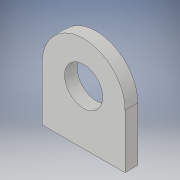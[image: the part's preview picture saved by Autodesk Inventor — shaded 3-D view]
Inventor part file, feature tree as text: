
AUTODESK INVENTOR PART (.ipt)
format: ipt  version: 2019 (Build 230136000, 136)  size: 108,544 bytes
history: native  units: mm
features: other x1, sketch x1, extrude x1, fillet x1, hole x1
ambient origin geometry x8: Origin, YZ Plane, XZ Plane, XY Plane, X Axis, Y Axis, Z Axis, Center Point
bodies: Body1 (feature_tree)
feature tree (5):
  other  "Bryła1"
  sketch  "Szkic1"
  extrude  "Wyciągnięcie proste1"  Depth=6.5mm
  fillet  "Zaokrąglenie1"  Radius=1.0mm
  hole  "Otwór1"  [1 undecoded]
note: 1 required parameter value undecoded (feature->parameter linkage not recoverable at this tier; creation-order binding heuristic only, values carry confidence <= 0.55)
